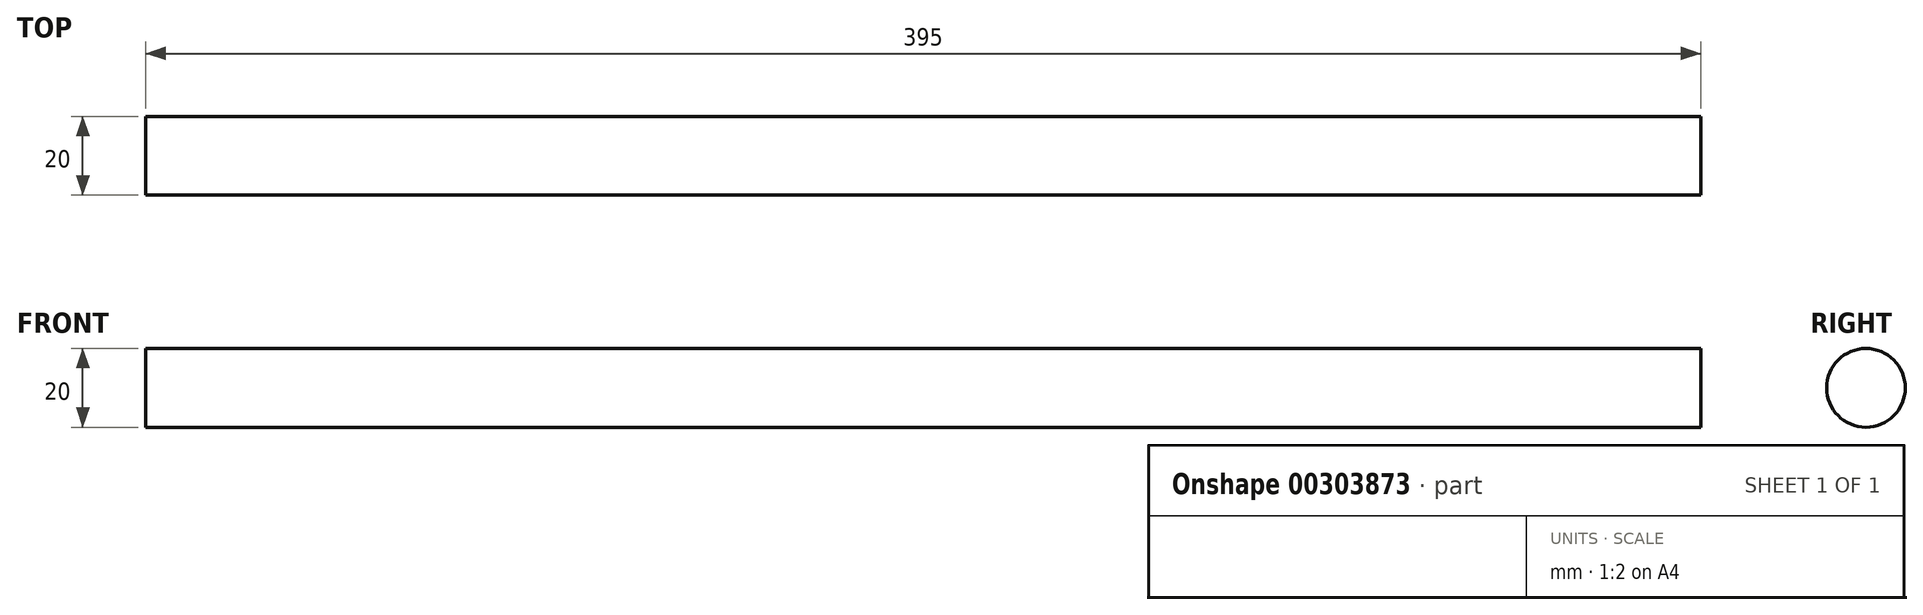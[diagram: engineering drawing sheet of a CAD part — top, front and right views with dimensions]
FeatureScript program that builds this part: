
annotation { "Feature Type Name" : "Feature", "Feature Type Description" : "" }
export const myFeature = defineFeature(function(context is Context, id is Id, definition is map)
    precondition{}
    {
        {
            var Q0;
            Q0=qCreatedBy(makeId("Right.planeOp"),FACE);
            var sketch = newSketch(context, id + "F0", { "sketchPlane" : qUnion([Q0])});
            skCircle(sketch, "E0", {"center": v(0, 0) * mm, "radius": 10 * mm});
            skSolve(sketch);
        }
        {
            var Q0;
            Q0=makeQuery(id+"F0.imprint","IMPRINT",FACE,{"disambiguationData":[TD([[makeQuery(id+"F0.imprint","IMPRINT",EDGE,{"derivedFrom":sQuery(id+"F0.wireOp",EDGE,"E0")}),1.0]])]});
            extrude(context, id + "F1", {"entities" : qUnion([Q0]), "endBound" : BoundingType.SYMMETRIC, "depth" : 395 * mm});
        }
    });
